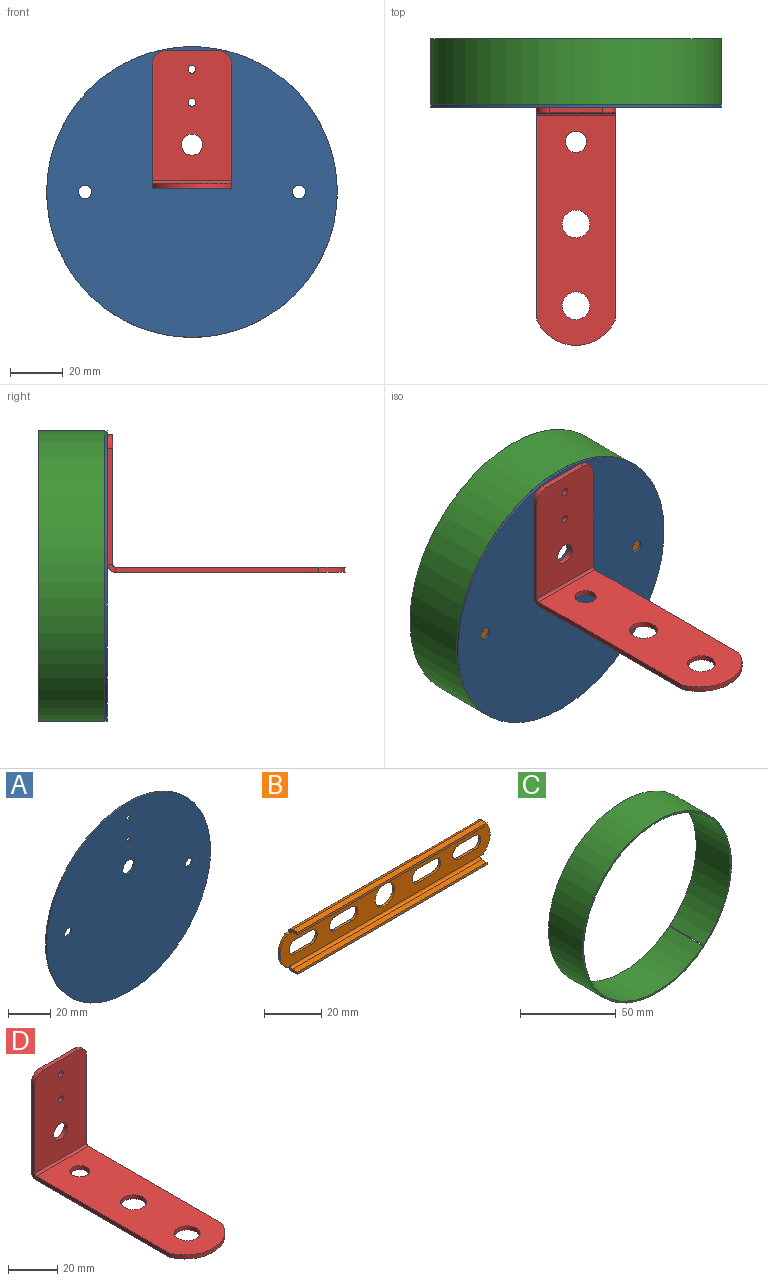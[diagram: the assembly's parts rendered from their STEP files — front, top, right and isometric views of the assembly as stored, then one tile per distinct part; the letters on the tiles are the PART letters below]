
ASSEMBLY  parts=4 mates=3
PART A: 8 faces, bbox 110x1x110 mm
  f0: cylinder r=2.5mm len=5mm, axis (0,-1,0), area 15.7mm2, adj f6,f7
  f1: cylinder r=2.5mm len=5mm, axis (0,-1,0), area 15.7mm2, adj f6,f7
  f2: cylinder r=1.5mm len=3mm, axis (0,-1,0), area 9.4mm2, adj f6,f7
  f3: cylinder r=1.5mm len=3mm, axis (0,-1,0), area 9.4mm2, adj f6,f7
  f4: cylinder r=4mm len=8mm, axis (0,-1,0), area 25.1mm2, adj f6,f7
  f5: cylinder r=55mm len=110mm, axis (0,-1,0), area 345.6mm2, adj f6,f7
  f6: plane 110x110mm, normal (0,1,0), area 9399.6mm2, adj f0,f1,f2,f3,f4,f5
  f7: plane 110x110mm, normal (0,-1,0), area 9399.6mm2, adj f0,f1,f2,f3,f4,f5
PART B: 43 faces, bbox 104x4.5x18 mm
  f0: plane 1.6x1mm, normal (0,0,-1), area 1.6mm2, adj f10,f23,f24,f40
  f1: plane 1.6x1mm, normal (0,0,1), area 1.6mm2, adj f8,f23,f24,f30
  f2: cylinder r=3mm len=6mm, axis (0,-1,0), area 9.4mm2, adj f3,f22,f23,f24
  f3: plane 8x1mm, normal (0,0,-1), area 8mm2, adj f2,f4,f23,f24
  f4: cylinder r=3mm len=6mm, axis (0,-1,0), area 9.4mm2, adj f3,f22,f23,f24
  f5: plane 8x1mm, normal (0,0,-1), area 8mm2, adj f6,f21,f23,f24
  f6: cylinder r=3mm len=6mm, axis (0,-1,0), area 9.4mm2, adj f5,f7,f23,f24
  f7: plane 8x1mm, normal (0,0,1), area 8mm2, adj f6,f21,f23,f24
  f8: cylinder r=8.9mm len=14mm, axis (0,-1,0), area 16.1mm2, adj f1,f20,f23,f24
  f9: plane 1.6x1mm, normal (0,0,1), area 1.6mm2, adj f10,f23,f24,f31
  f10: cylinder r=8.9mm len=14mm, axis (0,-1,0), area 16.1mm2, adj f0,f9,f23,f24
  f11: cylinder r=3mm len=6mm, axis (0,-1,0), area 9.4mm2, adj f12,f19,f23,f24
  f12: plane 8x1mm, normal (0,0,-1), area 8mm2, adj f11,f13,f23,f24
  f13: cylinder r=3mm len=6mm, axis (0,-1,0), area 9.4mm2, adj f12,f19,f23,f24
  f14: plane 8x1mm, normal (0,0,-1), area 8mm2, adj f15,f17,f23,f24
  f15: cylinder r=3mm len=6mm, axis (0,-1,0), area 9.4mm2, adj f14,f16,f23,f24
  f16: plane 8x1mm, normal (0,0,1), area 8mm2, adj f15,f17,f23,f24
  f17: cylinder r=3mm len=6mm, axis (0,-1,0), area 9.4mm2, adj f14,f16,f23,f24
  f18: cylinder r=4.75mm len=9.5mm, axis (0,-1,0), area 29.8mm2, adj f23,f24
  f19: plane 8x1mm, normal (0,0,1), area 8mm2, adj f11,f13,f23,f24
  f20: plane 1.6x1mm, normal (0,0,-1), area 1.6mm2, adj f8,f23,f24,f39
  f21: cylinder r=3mm len=6mm, axis (0,-1,0), area 9.4mm2, adj f5,f7,f23,f24
  f22: plane 8x1mm, normal (0,0,1), area 8mm2, adj f2,f4,f23,f24
  f23: plane 104x14mm, normal (0,1,0), area 1051.2mm2, adj f0,f1,f2,f3,f4,f5,f6,f7
  f24: plane 104x14mm, normal (0,-1,0), area 1051.2mm2, adj f0,f1,f2,f3,f4,f5,f6,f7
  f25: plane 94x1mm, normal (0,-1,0), area 94mm2, adj f26,f27,f28,f29
  f26: plane 2.5x1mm, normal (1,0,0), area 2.5mm2, adj f25,f28,f29,f31
  f27: plane 2.5x1mm, normal (-1,0,0), area 2.5mm2, adj f25,f28,f29,f30
  f28: plane 94x2.5mm, normal (0,0,1), area 235mm2, adj f25,f26,f27,f32
  f29: plane 94x2.5mm, normal (0,0,-1), area 235mm2, adj f25,f26,f27,f33
  f30: plane 2x2mm, normal (-1,0,0), area 2.4mm2, adj f1,f27,f32,f33
  f31: plane 2x2mm, normal (1,0,0), area 2.4mm2, adj f9,f26,f32,f33
  f32: cylinder r=2mm len=94mm, axis (-1,0,0), area 295.3mm2, adj f23,f28,f30,f31
  f33: cylinder r=1mm len=94mm, axis (-1,0,0), area 147.7mm2, adj f24,f29,f30,f31
  f34: plane 94x1mm, normal (0,-1,0), area 94mm2, adj f35,f36,f37,f38
  f35: plane 2.5x1mm, normal (-1,0,0), area 2.5mm2, adj f34,f37,f38,f39
  f36: plane 2.5x1mm, normal (1,0,0), area 2.5mm2, adj f34,f37,f38,f40
  f37: plane 94x2.5mm, normal (0,0,-1), area 235mm2, adj f34,f35,f36,f41
  f38: plane 94x2.5mm, normal (0,0,1), area 235mm2, adj f34,f35,f36,f42
  f39: plane 2x2mm, normal (-1,0,0), area 2.4mm2, adj f20,f35,f41,f42
  f40: plane 2x2mm, normal (1,0,0), area 2.4mm2, adj f0,f36,f41,f42
  f41: cylinder r=2mm len=94mm, axis (-1,0,0), area 295.3mm2, adj f23,f37,f39,f40
  f42: cylinder r=1mm len=94mm, axis (-1,0,0), area 147.7mm2, adj f24,f38,f39,f40
PART C: 6 faces, bbox 110x25x110 mm
  f0: plane 110x110mm, normal (0,1,0), area 341.9mm2, adj f1,f3,f4,f5
  f1: plane 25x0.78mm, normal (0.78,0,0.63), area 25mm2, adj f0,f2,f4,f5
  f2: plane 110x110mm, normal (0,-1,0), area 341.9mm2, adj f1,f3,f4,f5
  f3: plane 25x0.77mm, normal (-0.77,0,-0.64), area 25mm2, adj f0,f2,f4,f5
  f4: cylinder r=55mm len=110mm, axis (0,-1,0), area 8626.9mm2, adj f0,f1,f2,f3
  f5: cylinder r=54mm len=108mm, axis (0,-1,0), area 8470mm2, adj f0,f1,f2,f3
PART D: 22 faces, bbox 30x90x52 mm
  f0: plane 44x2mm, normal (-1,0,0), area 88mm2, adj f6,f7,f9,f18
  f1: plane 20x2mm, normal (0,0,1), area 40mm2, adj f6,f7,f8,f9
  f2: plane 44x2mm, normal (1,0,0), area 88mm2, adj f6,f7,f8,f19
  f3: cylinder r=1.5mm len=3mm, axis (0,-1,0), area 18.8mm2, adj f6,f7
  f4: cylinder r=1.5mm len=3mm, axis (0,-1,0), area 18.8mm2, adj f6,f7
  f5: cylinder r=4mm len=8mm, axis (0,-1,0), area 50.3mm2, adj f6,f7
  f6: plane 49x30mm, normal (0,1,0), area 1394.9mm2, adj f0,f1,f2,f3,f4,f5,f8,f9
  f7: plane 49x30mm, normal (0,-1,0), area 1394.9mm2, adj f0,f1,f2,f3,f4,f5,f8,f9
  f8: cylinder r=5mm len=5mm, axis (0,-1,0), area 15.7mm2, adj f1,f2,f6,f7
  f9: cylinder r=5mm len=5mm, axis (0,1,0), area 15.7mm2, adj f0,f1,f6,f7
  f10: plane 77x2mm, normal (1,0,0), area 154mm2, adj f11,f16,f17,f19
  f11: cylinder r=16.25mm len=30mm, axis (0,0,-1), area 76.4mm2, adj f10,f15,f16,f17
  f12: cylinder r=5.25mm len=10.5mm, axis (0,0,-1), area 66mm2, adj f16,f17
  f13: cylinder r=4mm len=8mm, axis (0,0,-1), area 50.3mm2, adj f16,f17
  f14: cylinder r=5.25mm len=10.5mm, axis (0,0,-1), area 66mm2, adj f16,f17
  f15: plane 77x2mm, normal (-1,0,0), area 154mm2, adj f11,f16,f17,f18
  f16: plane 87x30mm, normal (0,0,-1), area 2303.3mm2, adj f10,f11,f12,f13,f14,f15,f20
  f17: plane 87x30mm, normal (0,0,1), area 2303.3mm2, adj f10,f11,f12,f13,f14,f15,f21
  f18: plane 3x3mm, normal (-1,0,0), area 6.3mm2, adj f0,f15,f20,f21
  f19: plane 3x3mm, normal (1,0,0), area 6.3mm2, adj f2,f10,f20,f21
  f20: cylinder r=3mm len=30mm, axis (-1,0,0), area 141.4mm2, adj f6,f16,f18,f19
  f21: cylinder r=1mm len=30mm, axis (-1,0,0), area 47.1mm2, adj f7,f17,f18,f19
PLACE A t=(-29.17,-22.36,10.46)mm
PLACE B t=(-29.17,-17.86,10.46)mm
PLACE C t=(-29.17,2.64,10.46)mm
PLACE D t=(-29.17,-23.36,38.86)mm
MATE fastened D.f6 <-> A.f7  axis (0,1,0) through (-29.17,-23.36,39.46)mm
MATE fastened B.f18 <-> A.f5  axis (0,1,0) through (-29.17,-17.86,10.46)mm
MATE fastened A.f5 <-> C.f4  axis (0,1,0) through (-29.17,-22.36,10.46)mm
